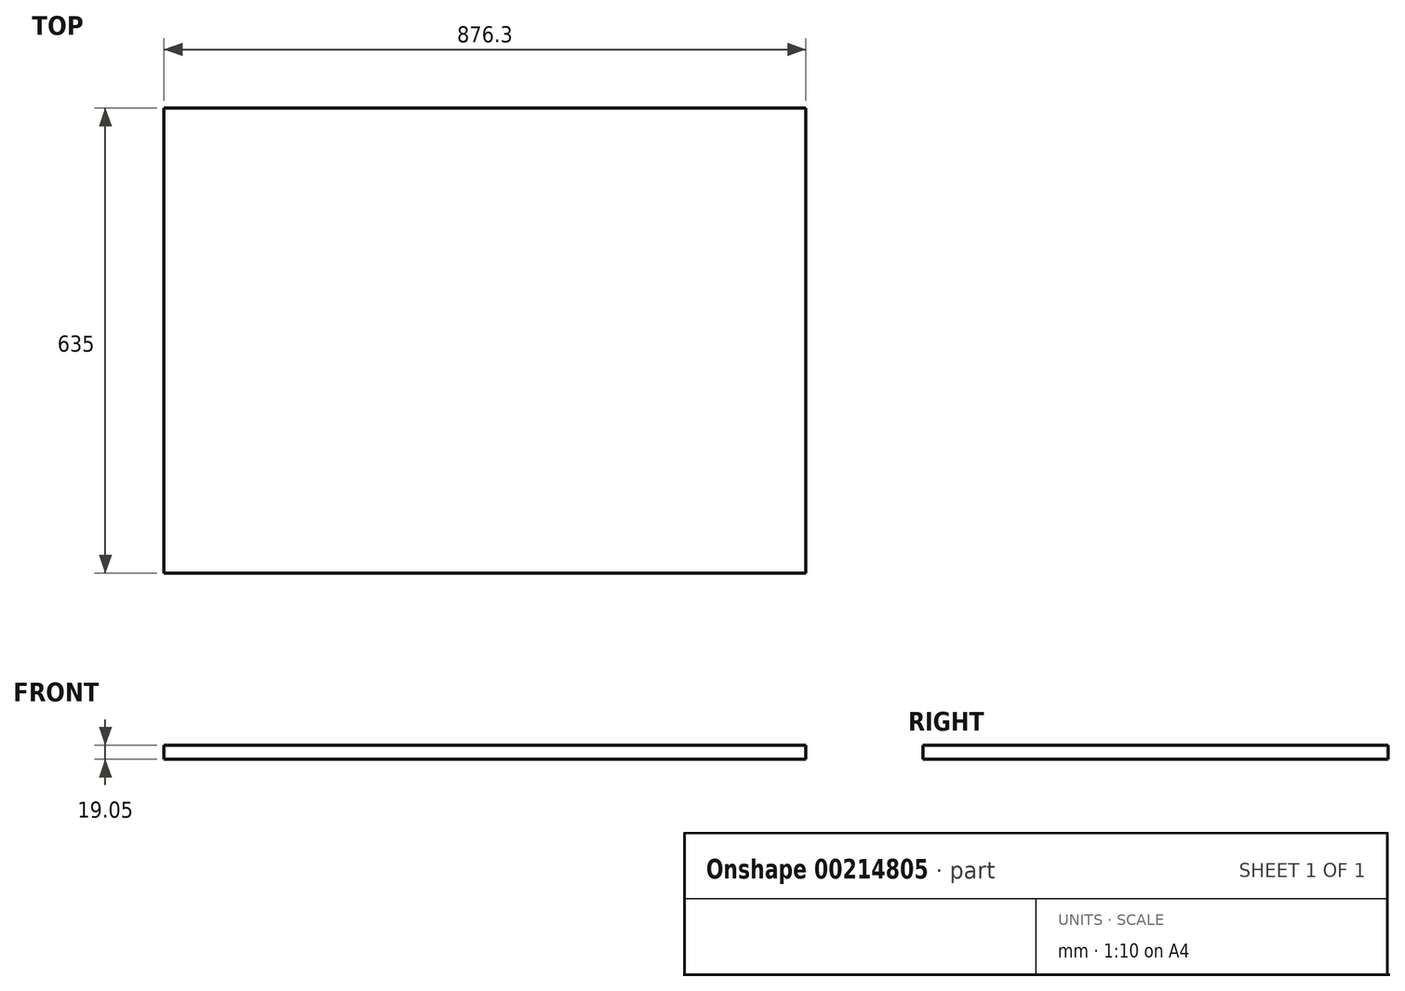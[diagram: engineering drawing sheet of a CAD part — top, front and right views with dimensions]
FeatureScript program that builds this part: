
annotation { "Feature Type Name" : "Feature", "Feature Type Description" : "" }
export const myFeature = defineFeature(function(context is Context, id is Id, definition is map)
    precondition{}
    {
        {
            var Q0;
            Q0=qCreatedBy(makeId("Top.planeOp"),FACE);
            var sketch = newSketch(context, id + "F0", { "sketchPlane" : qUnion([Q0])});
            skLineSegment(sketch, "E0.bottom", {"start": v(0, 0) * mm, "end": v(876.3, 0) * mm});
            skLineSegment(sketch, "E0.top", {"start": v(0, -635) * mm, "end": v(876.3, -635) * mm});
            skLineSegment(sketch, "E0.left", {"start": v(0, 0) * mm, "end": v(0, -635) * mm});
            skLineSegment(sketch, "E0.right", {"start": v(876.3, 0) * mm, "end": v(876.3, -635) * mm});
            skSolve(sketch);
        }
        {
            var Q0;
            Q0=makeQuery(id+"F0.imprint","IMPRINT",FACE,{"disambiguationData":[TD([[makeQuery(id+"F0.imprint","IMPRINT",EDGE,{"derivedFrom":sQuery(id+"F0.wireOp",EDGE,"E0.bottom")}),-1.0]])]});
            extrude(context, id + "F1", {"entities" : qUnion([Q0]), "depth" : 19.05 * mm});
        }
    });
